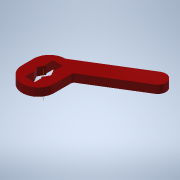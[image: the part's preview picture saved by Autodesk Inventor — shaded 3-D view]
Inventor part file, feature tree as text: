
AUTODESK INVENTOR PART (.ipt)
format: ipt  version: 2020 (Build 240168000, 168)  size: 123,904 bytes
history: native  units: mm
features: other x2, extrude x1, sketch x1
ambient origin geometry x8: Origin, YZ Plane, XZ Plane, XY Plane, X Axis, Y Axis, Z Axis, Center Point
bodies: Body1 (feature_tree)
feature tree (4):
  other  "Твердое тело1"
  extrude  "Выдавливание1"  Depth=5.0mm TaperAngle=0.0deg
  other  "РабОсь2"
  sketch  "Эскиз1"
